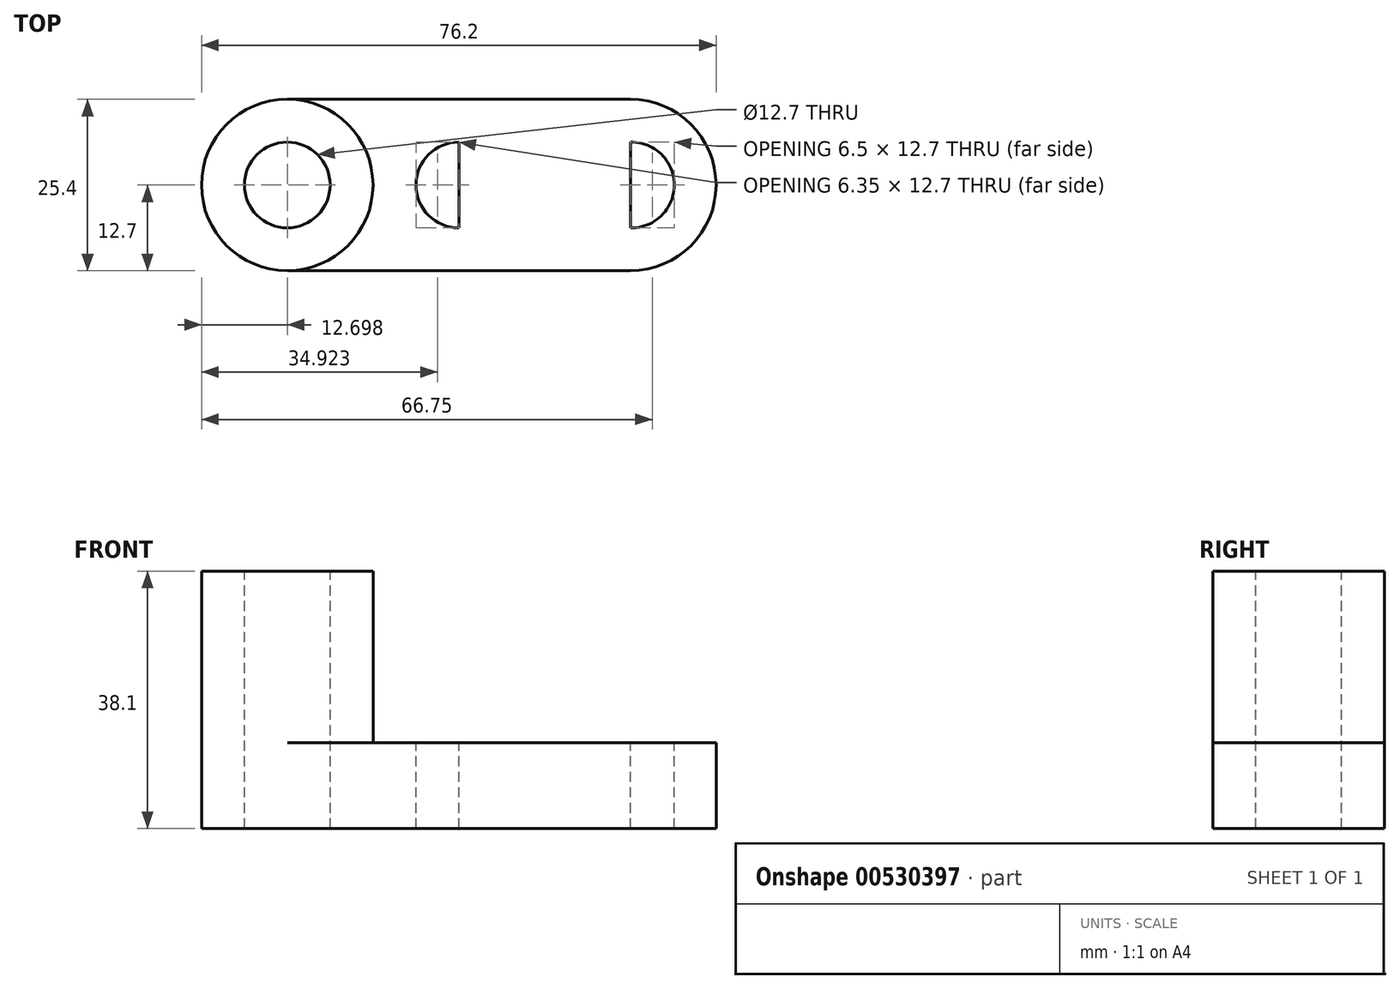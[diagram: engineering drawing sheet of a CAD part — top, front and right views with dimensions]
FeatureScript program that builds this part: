
annotation { "Feature Type Name" : "Feature", "Feature Type Description" : "" }
export const myFeature = defineFeature(function(context is Context, id is Id, definition is map)
    precondition{}
    {
        {
            var Q0;
            Q0=qCreatedBy(makeId("Front.planeOp"),FACE);
            var sketch = newSketch(context, id + "F0", { "sketchPlane" : qUnion([Q0])});
            skLineSegment(sketch, "E0", {"start": v(-18.33, 38.1) * mm, "end": v(-18.33, 0) * mm});
            skLineSegment(sketch, "E1", {"start": v(-18.33, 0) * mm, "end": v(57.87, 0) * mm});
            skLineSegment(sketch, "E2", {"start": v(-18.33, 38.1) * mm, "end": v(57.87, 38.1) * mm});
            skLineSegment(sketch, "E3", {"start": v(57.87, 38.1) * mm, "end": v(57.87, 0) * mm});
            skSolve(sketch);
        }
        {
            var Q0;
            Q0 = qSketchRegion(id + "F0", true);
            extrude(context, id + "F1", {"entities" : qUnion([Q0]), "depth" : 25.4 * mm, "offsetDistance" : 25.4 * mm});
        }
        {
            var Q0;
            Q0=makeQuery(id+"F1.opExtrude","CAP_FACE",FACE,{"disambiguationData":[OSD([sQuery(id+"F0.wireOp",EDGE,"E0"),sQuery(id+"F0.wireOp",EDGE,"E1"),sQuery(id+"F0.wireOp",EDGE,"E2"),sQuery(id+"F0.wireOp",EDGE,"E3")])],"isStart":false});
            var sketch = newSketch(context, id + "F2", { "sketchPlane" : qUnion([Q0])});
            skLineSegment(sketch, "E4", {"start": v(-18.33, 38.1) * mm, "end": v(7.07, 38.1) * mm});
            skLineSegment(sketch, "E5", {"start": v(7.07, 38.1) * mm, "end": v(7.07, 12.7) * mm});
            skLineSegment(sketch, "E6", {"start": v(7.07, 12.7) * mm, "end": v(57.87, 12.7) * mm});
            skLineSegment(sketch, "E7", {"start": v(57.87, 12.7) * mm, "end": v(57.87, 0) * mm});
            skLineSegment(sketch, "E8", {"start": v(57.87, 0) * mm, "end": v(-18.33, 0) * mm});
            skLineSegment(sketch, "E9", {"start": v(-18.33, 0) * mm, "end": v(-18.33, 38.1) * mm});
            skLineSegment(sketch, "E10", {"start": v(7.07, 38.1) * mm, "end": v(-18.33, 38.1) * mm});
            skSolve(sketch);
        }
        {
            var Q0;
            {var subQ0=sQuery(id+"F2.wireOp",EDGE,"E5");Q0=makeQuery(id+"F2.imprint","IMPRINT",FACE,{"disambiguationData":[TD([[makeQuery(id+"F2.imprint","IMPRINT",EDGE,{"derivedFrom":subQ0}),1.0]])]});}
            extrude(context, id + "F3", {"entities" : qUnion([Q0]), "operationType" : NewBodyOperationType.REMOVE, "endBound" : BoundingType.THROUGH_ALL, "oppositeDirection" : true, "depth" : 25.4 * mm, "offsetDistance" : 25.4 * mm});
        }
        {
            var Q0;
            Q0=makeQuery(id+"F1.opExtrude","SWEPT_FACE",FACE,{"disambiguationData":[OSD([sQuery(id+"F0.wireOp",EDGE,"E2")])]});
            var sketch = newSketch(context, id + "F4", { "sketchPlane" : qUnion([Q0])});
            skCircle(sketch, "E11", {"center": v(-5.63, -12.7) * mm, "radius": 12.7 * mm});
            skCircle(sketch, "E12", {"center": v(-5.63, -12.7) * mm, "radius": 6.35 * mm});
            skSolve(sketch);
        }
        {
            var Q0;
            {var subQ0=sQuery(id+"F4.wireOp",EDGE,"E11");var subQ1=sQuery(id+"F0.wireOp",EDGE,"E2");var subQ2=makeQuery(id+"F1.opExtrude","CAP_EDGE",EDGE,{"disambiguationData":[OSD([subQ1])],"isStart":true});var subQ3=makeQuery(id+"F4.imprint","INTERSECT",VERTEX,{"derivedFrom":[subQ2,subQ0]});Q0=makeQuery(id+"F4.imprint","IMPRINT",FACE,{"disambiguationData":[TD([[makeQuery(id+"F4.imprint","IMPRINT",EDGE,{"disambiguationData":[TD([[subQ3,1.0]])],"derivedFrom":subQ0}),-1.0]])]});}
            var Q1;
            {var subQ0=sQuery(id+"F4.wireOp",EDGE,"E11");var subQ1=sQuery(id+"F0.wireOp",EDGE,"E2");var subQ4=makeQuery(id+"F1.opExtrude","CAP_EDGE",EDGE,{"disambiguationData":[OSD([subQ1])],"isStart":false});var subQ5=makeQuery(id+"F4.imprint","INTERSECT",VERTEX,{"derivedFrom":[subQ4,subQ0]});Q1=makeQuery(id+"F4.imprint","IMPRINT",FACE,{"disambiguationData":[TD([[makeQuery(id+"F4.imprint","IMPRINT",EDGE,{"disambiguationData":[TD([[subQ5,-1.0]])],"derivedFrom":subQ0}),-1.0]])]});}
            var Q2;
            {var subQ0=sQuery(id+"F4.wireOp",EDGE,"E11");var subQ1=sQuery(id+"F0.wireOp",EDGE,"E2");var subQ2=makeQuery(id+"F1.opExtrude","CAP_EDGE",EDGE,{"disambiguationData":[OSD([subQ1])],"isStart":true});var subQ3=makeQuery(id+"F4.imprint","INTERSECT",VERTEX,{"derivedFrom":[subQ2,subQ0]});Q2=makeQuery(id+"F4.imprint","IMPRINT",FACE,{"disambiguationData":[TD([[makeQuery(id+"F4.imprint","IMPRINT",EDGE,{"disambiguationData":[TD([[subQ3,-1.0]])],"derivedFrom":subQ0}),-1.0]])]});}
            var Q3;
            {var subQ0=sQuery(id+"F4.wireOp",EDGE,"E11");var subQ1=sQuery(id+"F0.wireOp",EDGE,"E2");var subQ4=makeQuery(id+"F1.opExtrude","CAP_EDGE",EDGE,{"disambiguationData":[OSD([subQ1])],"isStart":false});var subQ5=makeQuery(id+"F4.imprint","INTERSECT",VERTEX,{"derivedFrom":[subQ4,subQ0]});Q3=makeQuery(id+"F4.imprint","IMPRINT",FACE,{"disambiguationData":[TD([[makeQuery(id+"F4.imprint","IMPRINT",EDGE,{"disambiguationData":[TD([[subQ5,1.0]])],"derivedFrom":subQ0}),-1.0]])]});}
            extrude(context, id + "F5", {"entities" : qUnion([Q0, Q1, Q2, Q3]), "operationType" : NewBodyOperationType.REMOVE, "oppositeDirection" : true, "depth" : 25.4 * mm, "offsetDistance" : 25.4 * mm});
        }
        {
            var Q0;
            {var subQ0=sQuery(id+"F0.wireOp",EDGE,"E2");var subQ1=makeQuery(id+"F1.opExtrude","CAP_EDGE",EDGE,{"disambiguationData":[OSD([subQ0])],"isStart":true});var subQ2=sQuery(id+"F0.wireOp",EDGE,"E0");var subQ3=makeQuery(id+"F1.opExtrude","SWEPT_EDGE",EDGE,{"disambiguationData":[OSD([subQ2,subQ0])]});var subQ4=makeQuery(id+"F4.imprint","INTERSECT",VERTEX,{"derivedFrom":[subQ3,subQ1]});var subQ5=sQuery(id+"F4.wireOp",EDGE,"E11");var subQ6=makeQuery(id+"F4.imprint","INTERSECT",VERTEX,{"derivedFrom":[subQ1,subQ5]});Q0=makeQuery(id+"F5.boolean.opBoolean","COPY",FACE,{"derivedFrom":makeQuery(id+"F5.opExtrude","CAP_FACE",FACE,{"disambiguationData":[OSD([subQ2,subQ0,subQ5]),TDD([makeQuery(id+"F4.imprint","IMPRINT",EDGE,{"disambiguationData":[TD([[subQ6,-1.0]])],"derivedFrom":subQ5}),makeQuery(id+"F4.imprint","IMPRINT",EDGE,{"disambiguationData":[TD([[subQ4,1.0]])],"derivedFrom":subQ3}),makeQuery(id+"F4.imprint","IMPRINT",EDGE,{"disambiguationData":[TD([[subQ6,1.0]])],"derivedFrom":subQ1})])],"isStart":false})});}
            var Q1;
            {var subQ0=sQuery(id+"F0.wireOp",EDGE,"E2");var subQ1=makeQuery(id+"F1.opExtrude","CAP_EDGE",EDGE,{"disambiguationData":[OSD([subQ0])],"isStart":false});var subQ2=sQuery(id+"F0.wireOp",EDGE,"E0");var subQ3=makeQuery(id+"F1.opExtrude","SWEPT_EDGE",EDGE,{"disambiguationData":[OSD([subQ2,subQ0])]});var subQ4=makeQuery(id+"F4.imprint","INTERSECT",VERTEX,{"derivedFrom":[subQ3,subQ1]});var subQ5=sQuery(id+"F4.wireOp",EDGE,"E11");var subQ6=makeQuery(id+"F4.imprint","INTERSECT",VERTEX,{"derivedFrom":[subQ1,subQ5]});Q1=makeQuery(id+"F5.boolean.opBoolean","COPY",FACE,{"derivedFrom":makeQuery(id+"F5.opExtrude","CAP_FACE",FACE,{"disambiguationData":[OSD([subQ2,subQ0,subQ5]),TDD([makeQuery(id+"F4.imprint","IMPRINT",EDGE,{"disambiguationData":[TD([[subQ6,1.0]])],"derivedFrom":subQ5}),makeQuery(id+"F4.imprint","IMPRINT",EDGE,{"disambiguationData":[TD([[subQ4,-1.0]])],"derivedFrom":subQ3}),makeQuery(id+"F4.imprint","IMPRINT",EDGE,{"disambiguationData":[TD([[subQ6,1.0]])],"derivedFrom":subQ1})])],"isStart":false})});}
            extrude(context, id + "F6", {"entities" : qUnion([Q0, Q1]), "operationType" : NewBodyOperationType.REMOVE, "endBound" : BoundingType.THROUGH_ALL, "oppositeDirection" : true, "depth" : 25.4 * mm, "offsetDistance" : 25.4 * mm});
        }
        {
            var Q0;
            Q0=makeQuery(id+"F1.opExtrude","SWEPT_FACE",FACE,{"disambiguationData":[OSD([sQuery(id+"F0.wireOp",EDGE,"E2")])]});
            var sketch = newSketch(context, id + "F7", { "sketchPlane" : qUnion([Q0])});
            skCircle(sketch, "E13", {"center": v(-5.63, -12.7) * mm, "radius": 6.35 * mm});
            skSolve(sketch);
        }
        {
            var Q0;
            Q0=makeQuery(id+"F7.imprint","IMPRINT",FACE,{"disambiguationData":[TD([[makeQuery(id+"F7.imprint","IMPRINT",EDGE,{"derivedFrom":sQuery(id+"F7.wireOp",EDGE,"E13")}),1.0]])]});
            extrude(context, id + "F8", {"entities" : qUnion([Q0]), "operationType" : NewBodyOperationType.REMOVE, "endBound" : BoundingType.THROUGH_ALL, "oppositeDirection" : true, "depth" : 25.4 * mm, "offsetDistance" : 25.4 * mm});
        }
        {
            var Q0;
            {var subQ0=sQuery(id+"F0.wireOp",EDGE,"E2");var subQ1=makeQuery(id+"F1.opExtrude","CAP_EDGE",EDGE,{"disambiguationData":[OSD([subQ0])],"isStart":false});var subQ2=sQuery(id+"F2.wireOp",EDGE,"E10");var subQ3=sQuery(id+"F2.wireOp",EDGE,"E5");var subQ4=makeQuery(id+"F3.boolean.opBoolean","COPY",EDGE,{"derivedFrom":makeQuery(id+"F3.opExtrude","SWEPT_EDGE",EDGE,{"disambiguationData":[OSD([subQ0,subQ3,subQ2])]})});var subQ5=makeQuery(id+"F4.imprint","INTERSECT",VERTEX,{"derivedFrom":[subQ4,subQ1]});var subQ6=sQuery(id+"F4.wireOp",EDGE,"E11");var subQ7=makeQuery(id+"F4.imprint","INTERSECT",VERTEX,{"derivedFrom":[subQ1,subQ6]});var subQ9=makeQuery(id+"F1.opExtrude","CAP_EDGE",EDGE,{"disambiguationData":[OSD([subQ0])],"isStart":true});var subQ10=makeQuery(id+"F4.imprint","INTERSECT",VERTEX,{"derivedFrom":[subQ4,subQ9]});var subQ11=makeQuery(id+"F4.imprint","INTERSECT",VERTEX,{"derivedFrom":[subQ9,subQ6]});Q0=makeQuery(id+"F5.boolean.opBoolean","MERGE",FACE,{"derivedFrom":[makeQuery(id+"F3.boolean.opBoolean","COPY",FACE,{"derivedFrom":makeQuery(id+"F3.opExtrude","SWEPT_FACE",FACE,{"disambiguationData":[OSD([sQuery(id+"F2.wireOp",EDGE,"E6")])]})})],"fromTools":[makeQuery(id+"F5.opExtrude","CAP_FACE",FACE,{"disambiguationData":[OSD([subQ0,subQ3,subQ2,subQ6]),TDD([makeQuery(id+"F4.imprint","IMPRINT",EDGE,{"disambiguationData":[TD([[subQ11,1.0]])],"derivedFrom":subQ6}),makeQuery(id+"F4.imprint","IMPRINT",EDGE,{"disambiguationData":[TD([[subQ10,-1.0]])],"derivedFrom":subQ4}),makeQuery(id+"F4.imprint","IMPRINT",EDGE,{"disambiguationData":[TD([[subQ11,-1.0]])],"derivedFrom":subQ9})])],"isStart":false}),makeQuery(id+"F5.opExtrude","CAP_FACE",FACE,{"disambiguationData":[OSD([subQ0,subQ3,subQ2,subQ6]),TDD([makeQuery(id+"F4.imprint","IMPRINT",EDGE,{"disambiguationData":[TD([[subQ7,-1.0]])],"derivedFrom":subQ6}),makeQuery(id+"F4.imprint","IMPRINT",EDGE,{"disambiguationData":[TD([[subQ5,1.0]])],"derivedFrom":subQ4}),makeQuery(id+"F4.imprint","IMPRINT",EDGE,{"disambiguationData":[TD([[subQ7,-1.0]])],"derivedFrom":subQ1})])],"isStart":false})]});}
            var sketch = newSketch(context, id + "F9", { "sketchPlane" : qUnion([Q0])});
            skLineSegment(sketch, "E14", {"start": v(7.07, -12.7) * mm, "end": v(57.87, -12.7) * mm});
            skLineSegment(sketch, "E15", {"start": v(7.07, -12.7) * mm, "end": v(19.77, -12.7) * mm});
            skLineSegment(sketch, "E16", {"start": v(57.87, -12.7) * mm, "end": v(45.17, -12.7) * mm});
            skLineSegment(sketch, "E17", {"start": v(19.77, -6.35) * mm, "end": v(19.77, -19.05) * mm});
            skLineSegment(sketch, "E18", {"start": v(19.77, -19.05) * mm, "end": v(45.17, -19.05) * mm});
            skLineSegment(sketch, "E19", {"start": v(45.17, -19.05) * mm, "end": v(45.17, -6.35) * mm});
            skLineSegment(sketch, "E20", {"start": v(45.17, -6.35) * mm, "end": v(19.77, -6.35) * mm});
            skLineSegment(sketch, "E21", {"start": v(45.17, 0) * mm, "end": v(57.87, 0) * mm});
            skLineSegment(sketch, "E22", {"start": v(45.17, 0) * mm, "end": v(45.17, -6.35) * mm});
            skLineSegment(sketch, "E23", {"start": v(45.17, -19.05) * mm, "end": v(45.17, -25.4) * mm});
            skLineSegment(sketch, "E24", {"start": v(45.17, -25.4) * mm, "end": v(57.87, -25.4) * mm});
            skArc(sketch, "E25", {"start": v(45.17, -19.05) * mm, "mid": v(51.67, -12.7) * mm, "end": v(45.17, -6.35) * mm});
            skArc(sketch, "E26", {"start": v(19.77, -6.35) * mm, "mid": v(13.42, -12.7) * mm, "end": v(19.77, -19.05) * mm});
            skArc(sketch, "E27", {"start": v(45.17, -25.4) * mm, "mid": v(57.87, -12.7) * mm, "end": v(45.17, 0) * mm});
            skSolve(sketch);
        }
        {
            var Q0;
            {var subQ0=sQuery(id+"F9.wireOp",EDGE,"E14");Q0=makeQuery(id+"F9.imprint","IMPRINT",FACE,{"disambiguationData":[TD([[makeQuery(id+"F9.imprint","IMPRINT",EDGE,{"derivedFrom":subQ0}),1.0]])]});}
            var Q1;
            {var subQ1=sQuery(id+"F9.wireOp",EDGE,"E15");var subQ3=sQuery(id+"F9.wireOp",EDGE,"E26");var subQ4=makeQuery(id+"F9.imprint","INTERSECT",VERTEX,{"derivedFrom":[subQ1,subQ3]});Q1=makeQuery(id+"F9.imprint","IMPRINT",FACE,{"disambiguationData":[TD([[makeQuery(id+"F9.imprint","IMPRINT",EDGE,{"disambiguationData":[TD([[subQ4,-1.0]])],"derivedFrom":subQ1}),1.0]])]});}
            var Q2;
            {var subQ1=sQuery(id+"F9.wireOp",EDGE,"E15");var subQ3=sQuery(id+"F9.wireOp",EDGE,"E26");var subQ4=makeQuery(id+"F9.imprint","INTERSECT",VERTEX,{"derivedFrom":[subQ1,subQ3]});Q2=makeQuery(id+"F9.imprint","IMPRINT",FACE,{"disambiguationData":[TD([[makeQuery(id+"F9.imprint","IMPRINT",EDGE,{"disambiguationData":[TD([[subQ4,-1.0]])],"derivedFrom":subQ1}),-1.0]])]});}
            var Q3;
            {var subQ0=sQuery(id+"F9.wireOp",EDGE,"E14");Q3=makeQuery(id+"F9.imprint","IMPRINT",FACE,{"disambiguationData":[TD([[makeQuery(id+"F9.imprint","IMPRINT",EDGE,{"derivedFrom":subQ0}),-1.0]])]});}
            var Q4;
            {var subQ1=sQuery(id+"F9.wireOp",EDGE,"E16");var subQ3=sQuery(id+"F9.wireOp",EDGE,"E25");var subQ4=makeQuery(id+"F9.imprint","INTERSECT",VERTEX,{"derivedFrom":[subQ1,subQ3]});Q4=makeQuery(id+"F9.imprint","IMPRINT",FACE,{"disambiguationData":[TD([[makeQuery(id+"F9.imprint","IMPRINT",EDGE,{"disambiguationData":[TD([[subQ4,-1.0]])],"derivedFrom":subQ1}),1.0]])]});}
            var Q5;
            {var subQ1=sQuery(id+"F9.wireOp",EDGE,"E16");var subQ3=sQuery(id+"F9.wireOp",EDGE,"E25");var subQ4=makeQuery(id+"F9.imprint","INTERSECT",VERTEX,{"derivedFrom":[subQ1,subQ3]});Q5=makeQuery(id+"F9.imprint","IMPRINT",FACE,{"disambiguationData":[TD([[makeQuery(id+"F9.imprint","IMPRINT",EDGE,{"disambiguationData":[TD([[subQ4,-1.0]])],"derivedFrom":subQ1}),-1.0]])]});}
            var Q6;
            {var subQ0=sQuery(id+"F9.wireOp",EDGE,"E21");Q6=makeQuery(id+"F9.imprint","IMPRINT",FACE,{"disambiguationData":[TD([[makeQuery(id+"F9.imprint","IMPRINT",EDGE,{"derivedFrom":subQ0}),-1.0]])]});}
            var Q7;
            {var subQ0=sQuery(id+"F9.wireOp",EDGE,"E24");Q7=makeQuery(id+"F9.imprint","IMPRINT",FACE,{"disambiguationData":[TD([[makeQuery(id+"F9.imprint","IMPRINT",EDGE,{"derivedFrom":subQ0}),1.0]])]});}
            extrude(context, id + "F10", {"entities" : qUnion([Q0, Q1, Q2, Q3, Q4, Q5, Q6, Q7]), "operationType" : NewBodyOperationType.REMOVE, "endBound" : BoundingType.THROUGH_ALL, "oppositeDirection" : true, "depth" : 25.4 * mm, "offsetDistance" : 25.4 * mm});
        }
    });
